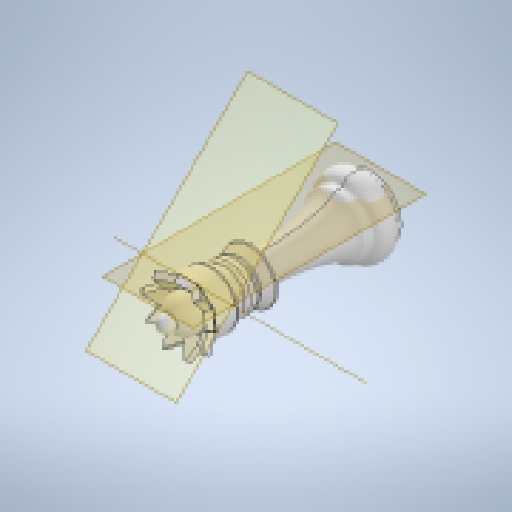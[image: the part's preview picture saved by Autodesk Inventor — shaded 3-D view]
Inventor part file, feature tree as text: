
AUTODESK INVENTOR PART (.ipt)
format: ipt  version: 2024.1 (Build 281209000, 209)  size: 1,048,576 bytes
history: native  units: mm
features: fillet x7, extrude x6, chamfer x6, sketch x6, plane x3, projected_geometry x2, other x1, revolve x1, pattern_circular x1
ambient origin geometry x8: Origin, YZ Plane, XZ Plane, XY Plane, X Axis, Y Axis, Z Axis, Center Point
bodies: Solid1 (feature_tree)
feature tree (33):
  extrude  "Extrusion1"  Depth=10.0mm TaperAngle=0.0deg
  other  "Work Axis1"
  extrude  "Extrusion2"  Depth=46.5mm
  revolve  "Revolution1"  [1 undecoded]
  chamfer  "Chamfer2"  Distance=3.0mm
  fillet  "Fillet1"  Radius=10.0mm
  fillet  "Fillet2"  Radius=4.15mm
  chamfer  "Chamfer3"  Distance=0.4mm
  chamfer  "Chamfer4"  Distance=2.489147mm
  fillet  "Fillet3"  Radius=7.875064mm
  fillet  "Fillet4"  Radius=5.915933mm
  fillet  "Fillet5"  Radius=0.487336mm
  plane  "Work Plane6"
  plane  "Work Plane7"
  plane  "Work Plane8"
  extrude  "Extrusion10"  Depth=0.3mm
  pattern_circular  "Circular Pattern5"  [2 undecoded]
  chamfer  "Chamfer5"  Distance=2.004443mm
  chamfer  "Chamfer6"  Distance=0.435462mm
  fillet  "Fillet7"  Radius=10.0mm
  fillet  "Fillet8"  Radius=8.1mm
  chamfer  "Chamfer1"  Distance=12.6mm
  sketch  "Sketch11"  dims[d9=0.5mm d10=2.0mm d11=45.0deg d40=10.0mm d41=0.0mm d42=4.15mm d43=0.0mm d44=0.4mm d45=0.0mm]
  extrude  "Extrusion6"  Depth=6.3mm
  extrude  "Extrusion7"  Depth=0.3mm
  extrude  "Extrusion8"  Depth=0.3mm
  sketch  "Sketch1"  dims[d0=10.0mm d1=3.0mm d2=0.0mm]
  sketch  "Sketch2"  dims[d3=3.65mm d4=46.5mm]
  sketch  "Sketch3"  dims[d5=360.0deg d6=14.3mm d7=3.0mm d8=0.0mm]
  projected_geometry  "Projected Loop1"
  sketch  "Sketch12"  dims[d51=6.042539mm]
  sketch  "Sketch15"  dims[d52=2.314913mm d53=2.489147mm d54=7.875064mm d55=5.915933mm d57=0.487336mm d58=0.259822mm d59=1.352868mm d60=2.004443mm d61=0.435462mm d64=10.0mm d65=0.0mm d74=8.1mm d75=12.6mm d76=6.3mm d78=5.2mm d79=0.4mm d80=4.4mm d81=9.4mm d82=4.7mm d83=8.9mm d84=10.56mm d85=5.28mm d86=3.17mm d87=10.36mm d88=5.18mm d89=12.3mm d90=6.15mm d91=2.2mm d92=1.5mm d93=2.03mm d94=1.6mm d95=3.17mm d96=6.108652mm d97=1.0mm d98=1.0mm d99=0.1mm d100=3.17mm d101=6.108652mm d102=1.45mm d103=2.0mm d104=6.108652mm d105=1.0mm d106=1.0mm d107=0.6mm d112=1.5mm d113=0.0mm d114=90.0mm d115=360.0deg d118=2.4mm d119=0.1mm d120=2.0mm d121=45.0deg d122=0.2mm d123=2.0mm d124=45.0deg d125=0.5mm d126=0.3mm]
  projected_geometry  "Projected Loop2"
note: 3 required parameter values undecoded (feature->parameter linkage not recoverable at this tier; creation-order binding heuristic only, values carry confidence <= 0.55)